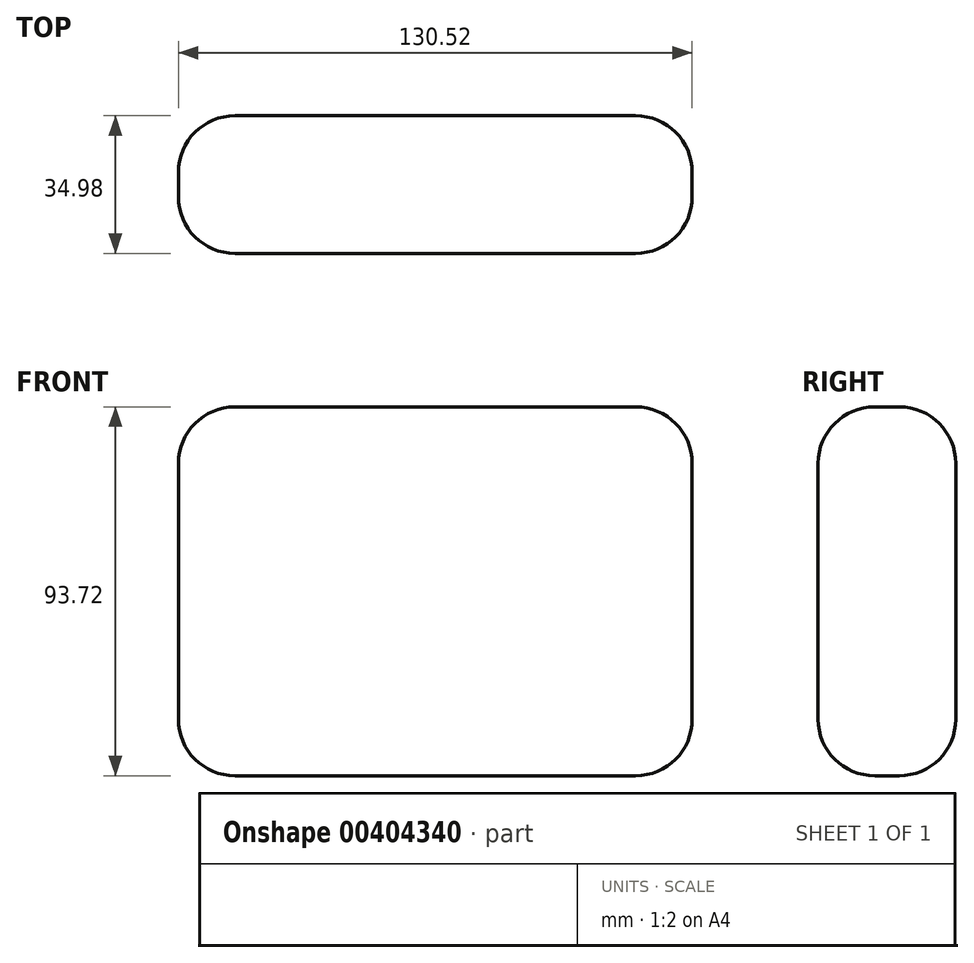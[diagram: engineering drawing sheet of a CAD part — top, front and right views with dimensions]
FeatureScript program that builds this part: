
annotation { "Feature Type Name" : "Feature", "Feature Type Description" : "" }
export const myFeature = defineFeature(function(context is Context, id is Id, definition is map)
    precondition{}
    {
        {
            var Q0;
            Q0=qCreatedBy(makeId("Top.planeOp"),FACE);
            var sketch = newSketch(context, id + "F0", { "sketchPlane" : qUnion([Q0])});
            skLineSegment(sketch, "E0.bottom", {"start": v(65.26, 17.49) * mm, "end": v(-65.26, 17.49) * mm});
            skLineSegment(sketch, "E0.top", {"start": v(65.26, -17.49) * mm, "end": v(-65.26, -17.49) * mm});
            skLineSegment(sketch, "E0.left", {"start": v(65.26, 17.49) * mm, "end": v(65.26, -17.49) * mm});
            skLineSegment(sketch, "E0.right", {"start": v(-65.26, 17.49) * mm, "end": v(-65.26, -17.49) * mm});
            skPoint(sketch, "E0.middle", {"position": v(0, 0) * mm});
            skSolve(sketch);
        }
        {
            var Q0;
            Q0 = qSketchRegion(id + "F0", true);
            extrude(context, id + "F1", {"entities" : qUnion([Q0]), "depth" : 93.72 * mm});
        }
        {
            var Q0;
            Q0=makeQuery(id+"F1.opExtrude","CAP_EDGE",EDGE,{"disambiguationData":[OSD([sQuery(id+"F0.wireOp",EDGE,"E0.bottom")])],"isStart":false});
            var Q1;
            Q1=makeQuery(id+"F1.opExtrude","CAP_EDGE",EDGE,{"disambiguationData":[OSD([sQuery(id+"F0.wireOp",EDGE,"E0.left")])],"isStart":false});
            var Q2;
            Q2=makeQuery(id+"F1.opExtrude","SWEPT_EDGE",EDGE,{"disambiguationData":[OSD([sQuery(id+"F0.wireOp",EDGE,"E0.bottom"),sQuery(id+"F0.wireOp",EDGE,"E0.left")])]});
            var Q3;
            Q3=makeQuery(id+"F1.opExtrude","CAP_EDGE",EDGE,{"disambiguationData":[OSD([sQuery(id+"F0.wireOp",EDGE,"E0.top")])],"isStart":false});
            var Q4;
            Q4=makeQuery(id+"F1.opExtrude","CAP_EDGE",EDGE,{"disambiguationData":[OSD([sQuery(id+"F0.wireOp",EDGE,"E0.right")])],"isStart":false});
            var Q5;
            Q5=makeQuery(id+"F1.opExtrude","SWEPT_EDGE",EDGE,{"disambiguationData":[OSD([sQuery(id+"F0.wireOp",EDGE,"E0.bottom"),sQuery(id+"F0.wireOp",EDGE,"E0.right")])]});
            var Q6;
            Q6=makeQuery(id+"F1.opExtrude","CAP_EDGE",EDGE,{"disambiguationData":[OSD([sQuery(id+"F0.wireOp",EDGE,"E0.bottom")])],"isStart":true});
            var Q7;
            Q7=makeQuery(id+"F1.opExtrude","CAP_EDGE",EDGE,{"disambiguationData":[OSD([sQuery(id+"F0.wireOp",EDGE,"E0.top")])],"isStart":true});
            var Q8;
            Q8=makeQuery(id+"F1.opExtrude","SWEPT_EDGE",EDGE,{"disambiguationData":[OSD([sQuery(id+"F0.wireOp",EDGE,"E0.top"),sQuery(id+"F0.wireOp",EDGE,"E0.left")])]});
            var Q9;
            Q9=makeQuery(id+"F1.opExtrude","CAP_EDGE",EDGE,{"disambiguationData":[OSD([sQuery(id+"F0.wireOp",EDGE,"E0.left")])],"isStart":true});
            var Q10;
            Q10=makeQuery(id+"F1.opExtrude","CAP_EDGE",EDGE,{"disambiguationData":[OSD([sQuery(id+"F0.wireOp",EDGE,"E0.right")])],"isStart":true});
            var Q11;
            Q11=makeQuery(id+"F1.opExtrude","SWEPT_EDGE",EDGE,{"disambiguationData":[OSD([sQuery(id+"F0.wireOp",EDGE,"E0.top"),sQuery(id+"F0.wireOp",EDGE,"E0.right")])]});
            fillet(context, id + "F2", {"entities" : qUnion([Q0, Q1, Q2, Q3, Q4, Q5, Q6, Q7, Q8, Q9, Q10, Q11]), "radius" : 14.37 * mm, "tangentPropagation" : true, "allowEdgeOverflow" : false});
        }
    });
